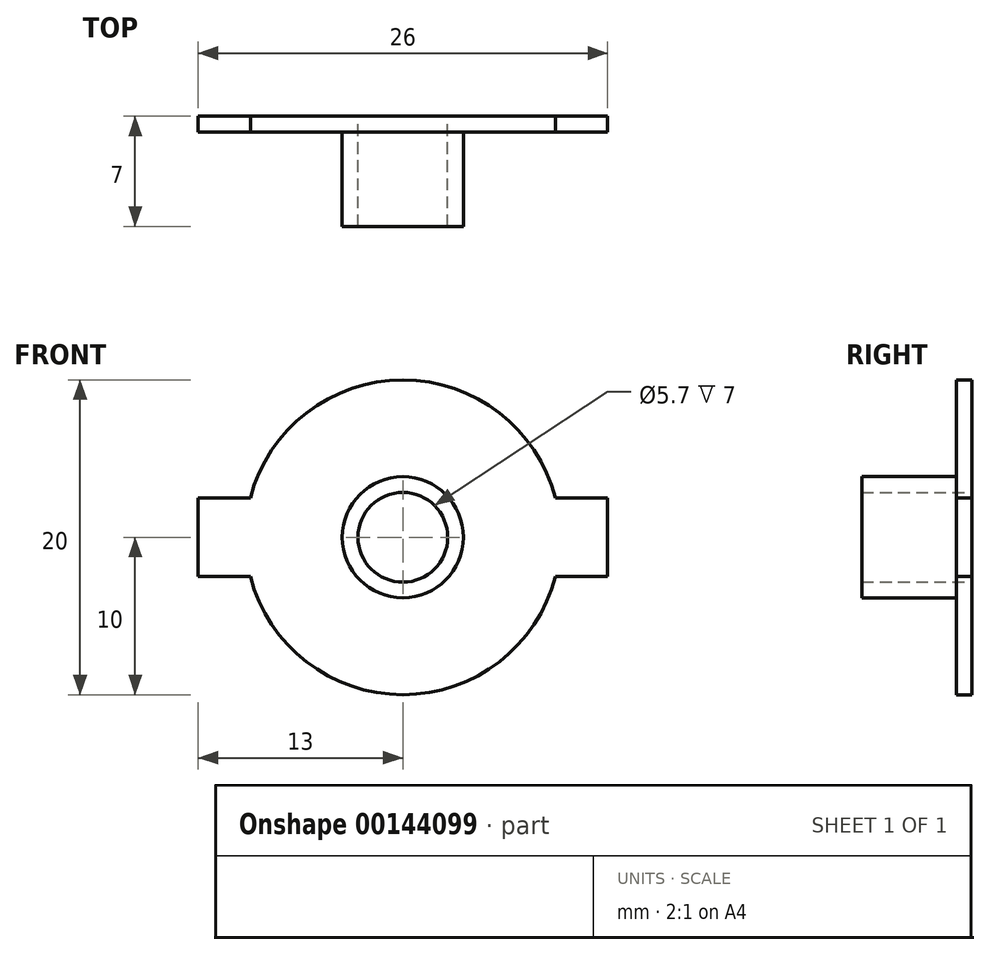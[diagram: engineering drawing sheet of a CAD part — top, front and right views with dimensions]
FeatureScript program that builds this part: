
annotation { "Feature Type Name" : "Feature", "Feature Type Description" : "" }
export const myFeature = defineFeature(function(context is Context, id is Id, definition is map)
    precondition{}
    {
        {
            var Q0;
            Q0=qCreatedBy(makeId("Front.planeOp"),FACE);
            var sketch = newSketch(context, id + "F0", { "sketchPlane" : qUnion([Q0])});
            skCircle(sketch, "E0", {"center": v(0, 0) * mm, "radius": 10 * mm});
            skSolve(sketch);
        }
        {
            var Q0;
            Q0=makeQuery(id+"F0.imprint","IMPRINT",FACE,{"disambiguationData":[TD([[makeQuery(id+"F0.imprint","IMPRINT",EDGE,{"derivedFrom":sQuery(id+"F0.wireOp",EDGE,"E0")}),1.0]])]});
            extrude(context, id + "F1", {"entities" : qUnion([Q0]), "depth" : 1 * mm});
        }
        {
            var Q0;
            Q0=makeQuery(id+"F1.opExtrude","CAP_FACE",FACE,{"disambiguationData":[OSD([sQuery(id+"F0.wireOp",EDGE,"E0")])],"isStart":false});
            var sketch = newSketch(context, id + "F2", { "sketchPlane" : qUnion([Q0])});
            skSolve(sketch);
        }
        {
            var Q0;
            Q0=makeQuery(id+"F1.opExtrude","CAP_FACE",FACE,{"disambiguationData":[OSD([sQuery(id+"F0.wireOp",EDGE,"E0")])],"isStart":true});
            var sketch = newSketch(context, id + "F3", { "sketchPlane" : qUnion([Q0])});
            skLineSegment(sketch, "E1.bottom", {"start": v(13, -2.5) * mm, "end": v(-13, -2.5) * mm});
            skLineSegment(sketch, "E1.top", {"start": v(13, 2.5) * mm, "end": v(-13, 2.5) * mm});
            skLineSegment(sketch, "E1.left", {"start": v(13, -2.5) * mm, "end": v(13, 2.5) * mm});
            skLineSegment(sketch, "E1.right", {"start": v(-13, -2.5) * mm, "end": v(-13, 2.5) * mm});
            skPoint(sketch, "E1.middle", {"position": v(0, 0) * mm});
            skSolve(sketch);
        }
        {
            var Q0;
            Q0 = qSketchRegion(id + "F3", true);
            extrude(context, id + "F4", {"entities" : qUnion([Q0]), "operationType" : NewBodyOperationType.ADD, "oppositeDirection" : true, "depth" : 1 * mm});
        }
        {
            var Q0;
            Q0=makeQuery(id+"F2.imprint","IMPRINT",FACE,{"disambiguationData":[TD([[makeQuery(id+"F2.imprint","IMPRINT",EDGE,{"derivedFrom":makeQuery(id+"F1.opExtrude","CAP_EDGE",EDGE,{"disambiguationData":[OSD([sQuery(id+"F0.wireOp",EDGE,"E0")])],"isStart":false})}),1.0]])]});
            var sketch = newSketch(context, id + "F5", { "sketchPlane" : qUnion([Q0])});
            skCircle(sketch, "E2", {"center": v(0, 0) * mm, "radius": 2.85 * mm});
            skCircle(sketch, "E3.0", {"center": v(0, 0) * mm, "radius": 3.85 * mm});
            skSolve(sketch);
        }
        {
            var Q0;
            Q0=makeQuery(id+"F2.imprint","IMPRINT",FACE,{"disambiguationData":[TD([[makeQuery(id+"F2.imprint","IMPRINT",EDGE,{"derivedFrom":makeQuery(id+"F1.opExtrude","CAP_EDGE",EDGE,{"disambiguationData":[OSD([sQuery(id+"F0.wireOp",EDGE,"E0")])],"isStart":false})}),1.0]])]});
            var sketch = newSketch(context, id + "F6", { "sketchPlane" : qUnion([Q0])});
            skCircle(sketch, "E4", {"center": v(0, 0) * mm, "radius": 2.85 * mm});
            skSolve(sketch);
        }
        {
            var Q0;
            Q0=qSketchRegion(id+"F5",true);
            extrude(context, id + "F7", {"entities" : qUnion([Q0]), "operationType" : NewBodyOperationType.ADD, "depth" : 6 * mm});
        }
        {
            var Q0;
            Q0=qSketchRegion(id+"F6",true);
            extrude(context, id + "F8", {"entities" : qUnion([Q0]), "operationType" : NewBodyOperationType.REMOVE, "endBound" : BoundingType.THROUGH_ALL, "depth" : 25 * mm, "hasSecondDirection" : true, "secondDirectionBound" : SecondDirectionBoundingType.THROUGH_ALL, "secondDirectionOppositeDirection" : true, "secondDirectionDepth" : 25 * mm});
        }
    });
